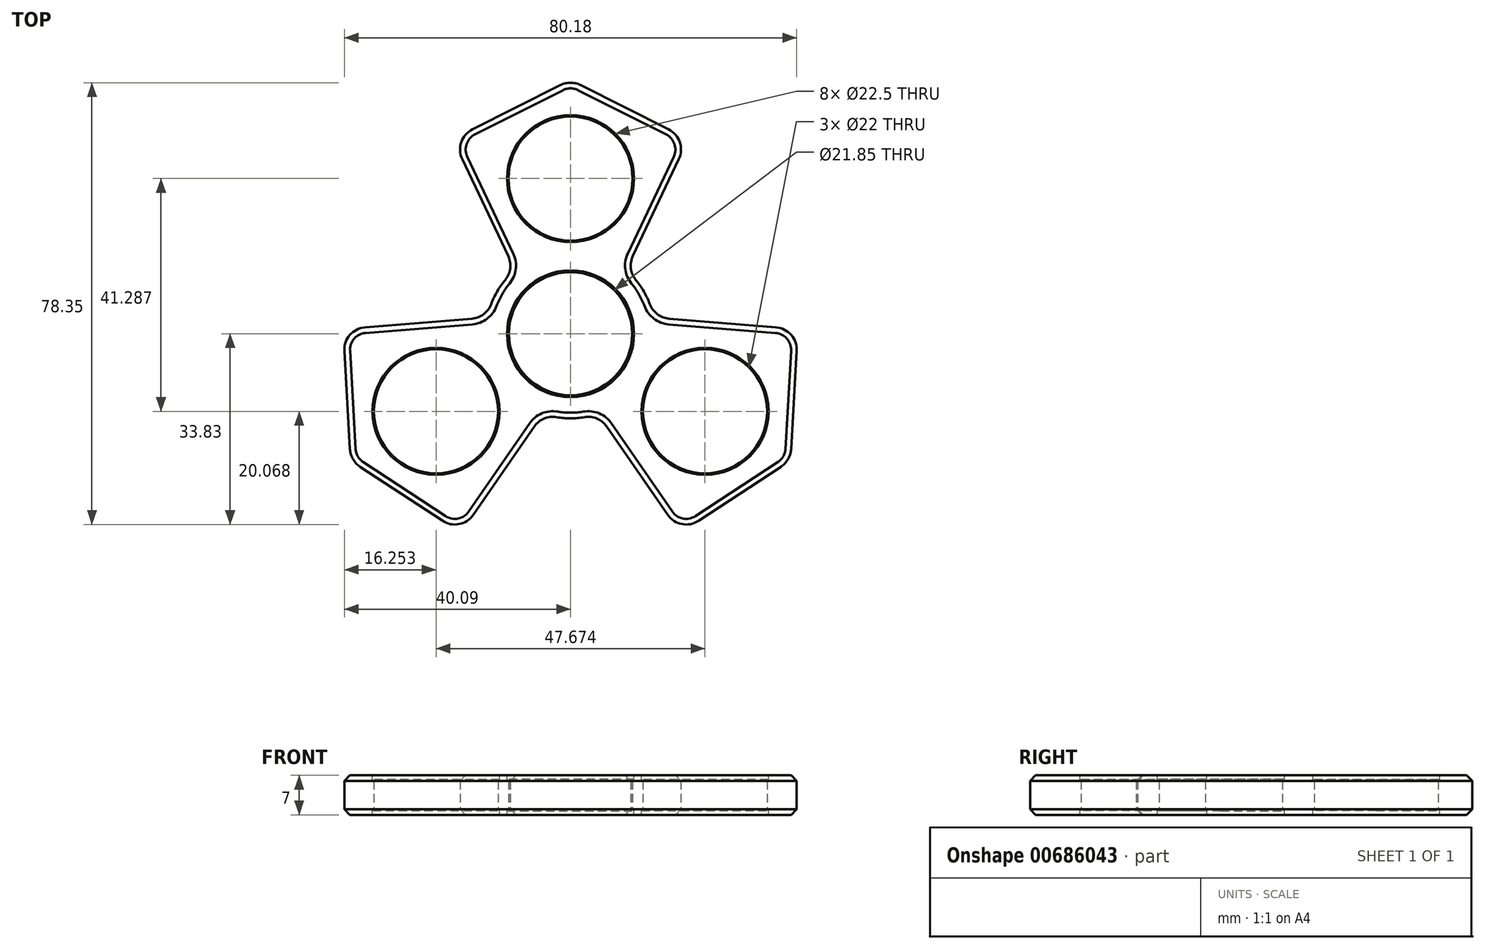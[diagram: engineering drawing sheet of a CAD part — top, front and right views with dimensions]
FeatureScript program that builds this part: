
annotation { "Feature Type Name" : "Feature", "Feature Type Description" : "" }
export const myFeature = defineFeature(function(context is Context, id is Id, definition is map)
    precondition{}
    {
        {
            var Q0;
            Q0=qCreatedBy(makeId("Top.planeOp"),FACE);
            var sketch = newSketch(context, id + "F0", { "sketchPlane" : qUnion([Q0])});
            skCircle(sketch, "E0", {"center": v(0, 0) * mm, "radius": 4 * mm});
            skCircle(sketch, "E1", {"center": v(0, 0) * mm, "radius": 45 * mm, "construction": true});
            skCircle(sketch, "E2", {"center": v(0, 27.52) * mm, "radius": 4 * mm});
            skLineSegment(sketch, "E3", {"start": v(0, 45) * mm, "end": v(-20.87, 34.5) * mm});
            skLineSegment(sketch, "E4", {"start": v(-20.87, 34.5) * mm, "end": v(-9.86, 11.3) * mm});
            skLineSegment(sketch, "E5.MirrorCS", {"start": v(0, 45) * mm, "end": v(20.87, 34.5) * mm});
            skLineSegment(sketch, "E6.MirrorCS", {"start": v(20.87, 34.5) * mm, "end": v(9.86, 11.3) * mm});
            skCircle(sketch, "E7", {"center": v(0, 0) * mm, "radius": 15 * mm});
            skCircle(sketch, "E8.1.1", {"center": v(0, 27.52) * mm, "radius": 11 * mm});
            skCircle(sketch, "E9", {"center": v(0, 0) * mm, "radius": 10.93 * mm});
            skLineSegment(sketch, "E10.1.0", {"start": v(-40.3, 0.83) * mm, "end": v(-14.72, 2.89) * mm});
            skLineSegment(sketch, "E10.1.1", {"start": v(-38.97, -22.5) * mm, "end": v(-40.3, 0.83) * mm});
            skLineSegment(sketch, "E10.1.2", {"start": v(-38.97, -22.5) * mm, "end": v(-19.43, -35.32) * mm});
            skLineSegment(sketch, "E10.1.3", {"start": v(-19.43, -35.32) * mm, "end": v(-4.86, -14.2) * mm});
            skCircle(sketch, "E10.1.4", {"center": v(-23.84, -13.76) * mm, "radius": 11 * mm});
            skCircle(sketch, "E10.1.5", {"center": v(-23.84, -13.76) * mm, "radius": 4 * mm});
            skLineSegment(sketch, "E10.2.0", {"start": v(19.43, -35.32) * mm, "end": v(4.86, -14.2) * mm});
            skLineSegment(sketch, "E10.2.1", {"start": v(38.97, -22.5) * mm, "end": v(19.43, -35.32) * mm});
            skLineSegment(sketch, "E10.2.2", {"start": v(38.97, -22.5) * mm, "end": v(40.3, 0.83) * mm});
            skLineSegment(sketch, "E10.2.3", {"start": v(40.3, 0.83) * mm, "end": v(14.72, 2.89) * mm});
            skCircle(sketch, "E10.2.4", {"center": v(23.84, -13.76) * mm, "radius": 11 * mm});
            skCircle(sketch, "E10.2.5", {"center": v(23.84, -13.76) * mm, "radius": 4 * mm});
            skSolve(sketch);
        }
        {
            var Q0;
            Q0=qSketchRegion(id+"F0",true);
            extrude(context, id + "F1", {"entities" : qUnion([Q0]), "depth" : 7 * mm, "offsetDistance" : 25 * mm});
        }
        {
            var Q0;
            Q0=makeQuery(id+"F1.opExtrude","SWEPT_EDGE",EDGE,{"disambiguationData":[OSD([sQuery(id+"F0.wireOp",EDGE,"472c968c-1dea-4124-b28b-64800f5080bb.1.0"),sQuery(id+"F0.wireOp",EDGE,"472c968c-1dea-4124-b28b-64800f5080bb.1.1")])]});
            var Q1;
            Q1=makeQuery(id+"F1.opExtrude","SWEPT_EDGE",EDGE,{"disambiguationData":[OSD([sQuery(id+"F0.wireOp",EDGE,"472c968c-1dea-4124-b28b-64800f5080bb.2.2"),sQuery(id+"F0.wireOp",EDGE,"472c968c-1dea-4124-b28b-64800f5080bb.2.3")])]});
            var Q2;
            Q2=makeQuery(id+"F1.opExtrude","SWEPT_EDGE",EDGE,{"disambiguationData":[OSD([sQuery(id+"F0.wireOp",EDGE,"472c968c-1dea-4124-b28b-64800f5080bb.2.0"),sQuery(id+"F0.wireOp",EDGE,"472c968c-1dea-4124-b28b-64800f5080bb.2.2")])]});
            var Q3;
            Q3=makeQuery(id+"F1.opExtrude","SWEPT_EDGE",EDGE,{"disambiguationData":[OSD([sQuery(id+"F0.wireOp",EDGE,"472c968c-1dea-4124-b28b-64800f5080bb.2.0"),sQuery(id+"F0.wireOp",EDGE,"472c968c-1dea-4124-b28b-64800f5080bb.2.1")])]});
            var Q4;
            Q4=makeQuery(id+"F1.opExtrude","SWEPT_EDGE",EDGE,{"disambiguationData":[OSD([sQuery(id+"F0.wireOp",EDGE,"472c968c-1dea-4124-b28b-64800f5080bb.2.1"),sQuery(id+"F0.wireOp",EDGE,"E7")])]});
            var Q5;
            Q5=makeQuery(id+"F1.opExtrude","SWEPT_EDGE",EDGE,{"disambiguationData":[OSD([sQuery(id+"F0.wireOp",EDGE,"E6.MirrorCS"),sQuery(id+"F0.wireOp",EDGE,"E7")])]});
            var Q6;
            Q6=makeQuery(id+"F1.opExtrude","SWEPT_EDGE",EDGE,{"disambiguationData":[OSD([sQuery(id+"F0.wireOp",EDGE,"E5.MirrorCS"),sQuery(id+"F0.wireOp",EDGE,"E6.MirrorCS")])]});
            var Q7;
            Q7=makeQuery(id+"F1.opExtrude","SWEPT_EDGE",EDGE,{"disambiguationData":[OSD([sQuery(id+"F0.wireOp",EDGE,"E3"),sQuery(id+"F0.wireOp",EDGE,"E5.MirrorCS")])]});
            var Q8;
            Q8=makeQuery(id+"F1.opExtrude","SWEPT_EDGE",EDGE,{"disambiguationData":[OSD([sQuery(id+"F0.wireOp",EDGE,"E3"),sQuery(id+"F0.wireOp",EDGE,"E4")])]});
            var Q9;
            Q9=makeQuery(id+"F1.opExtrude","SWEPT_EDGE",EDGE,{"disambiguationData":[OSD([sQuery(id+"F0.wireOp",EDGE,"E4"),sQuery(id+"F0.wireOp",EDGE,"E7")])]});
            var Q10;
            Q10=makeQuery(id+"F1.opExtrude","SWEPT_EDGE",EDGE,{"disambiguationData":[OSD([sQuery(id+"F0.wireOp",EDGE,"472c968c-1dea-4124-b28b-64800f5080bb.1.3"),sQuery(id+"F0.wireOp",EDGE,"E7")])]});
            var Q11;
            Q11=makeQuery(id+"F1.opExtrude","SWEPT_EDGE",EDGE,{"disambiguationData":[OSD([sQuery(id+"F0.wireOp",EDGE,"472c968c-1dea-4124-b28b-64800f5080bb.1.2"),sQuery(id+"F0.wireOp",EDGE,"472c968c-1dea-4124-b28b-64800f5080bb.1.3")])]});
            var Q12;
            Q12=makeQuery(id+"F1.opExtrude","SWEPT_EDGE",EDGE,{"disambiguationData":[OSD([sQuery(id+"F0.wireOp",EDGE,"472c968c-1dea-4124-b28b-64800f5080bb.1.0"),sQuery(id+"F0.wireOp",EDGE,"472c968c-1dea-4124-b28b-64800f5080bb.1.2")])]});
            var Q13;
            Q13=makeQuery(id+"F1.opExtrude","SWEPT_EDGE",EDGE,{"disambiguationData":[OSD([sQuery(id+"F0.wireOp",EDGE,"472c968c-1dea-4124-b28b-64800f5080bb.1.1"),sQuery(id+"F0.wireOp",EDGE,"E7")])]});
            var Q14;
            Q14=makeQuery(id+"F1.opExtrude","SWEPT_EDGE",EDGE,{"disambiguationData":[OSD([sQuery(id+"F0.wireOp",EDGE,"472c968c-1dea-4124-b28b-64800f5080bb.2.3"),sQuery(id+"F0.wireOp",EDGE,"E7")])]});
            var Q15;
            Q15=makeQuery(id+"F1.opExtrude","SWEPT_EDGE",EDGE,{"disambiguationData":[OSD([sQuery(id+"F0.wireOp",EDGE,"E10.2.0"),sQuery(id+"F0.wireOp",EDGE,"E10.2.1")])]});
            var Q16;
            Q16=makeQuery(id+"F1.opExtrude","SWEPT_EDGE",EDGE,{"disambiguationData":[OSD([sQuery(id+"F0.wireOp",EDGE,"E10.2.1"),sQuery(id+"F0.wireOp",EDGE,"E10.2.2")])]});
            var Q17;
            Q17=makeQuery(id+"F1.opExtrude","SWEPT_EDGE",EDGE,{"disambiguationData":[OSD([sQuery(id+"F0.wireOp",EDGE,"E10.2.2"),sQuery(id+"F0.wireOp",EDGE,"E10.2.3")])]});
            var Q18;
            Q18=makeQuery(id+"F1.opExtrude","SWEPT_EDGE",EDGE,{"disambiguationData":[OSD([sQuery(id+"F0.wireOp",EDGE,"E10.1.2"),sQuery(id+"F0.wireOp",EDGE,"E10.1.3")])]});
            var Q19;
            Q19=makeQuery(id+"F1.opExtrude","SWEPT_EDGE",EDGE,{"disambiguationData":[OSD([sQuery(id+"F0.wireOp",EDGE,"E10.1.1"),sQuery(id+"F0.wireOp",EDGE,"E10.1.2")])]});
            var Q20;
            Q20=makeQuery(id+"F1.opExtrude","SWEPT_EDGE",EDGE,{"disambiguationData":[OSD([sQuery(id+"F0.wireOp",EDGE,"E10.1.0"),sQuery(id+"F0.wireOp",EDGE,"E10.1.1")])]});
            fillet(context, id + "F2", {"entities" : qUnion([Q0, Q1, Q2, Q3, Q4, Q5, Q6, Q7, Q8, Q9, Q10, Q11, Q12, Q13, Q14, Q15, Q16, Q17, Q18, Q19, Q20]), "radius" : 4 * mm, "tangentPropagation" : true, "allowEdgeOverflow" : false});
        }
        {
            var Q0;
            Q0=makeQuery(id+"F1.opExtrude","CAP_EDGE",EDGE,{"disambiguationData":[OSD([sQuery(id+"F0.wireOp",EDGE,"E4")])],"isStart":false});
            var Q1;
            Q1=makeQuery(id+"F1.opExtrude","CAP_EDGE",EDGE,{"disambiguationData":[OSD([sQuery(id+"F0.wireOp",EDGE,"E4")])],"isStart":true});
            var Q2;
            Q2=makeQuery(id+"F1.opExtrude","CAP_EDGE",EDGE,{"disambiguationData":[OSD([sQuery(id+"F0.wireOp",EDGE,"E10.1.1")])],"isStart":false});
            var Q3;
            Q3=makeQuery(id+"F1.opExtrude","CAP_EDGE",EDGE,{"disambiguationData":[OSD([sQuery(id+"F0.wireOp",EDGE,"E10.1.2")])],"isStart":false});
            var Q4;
            Q4=makeQuery(id+"F1.opExtrude","CAP_FACE",FACE,{"disambiguationData":[OSD([sQuery(id+"F0.wireOp",EDGE,"E3"),sQuery(id+"F0.wireOp",EDGE,"E4"),sQuery(id+"F0.wireOp",EDGE,"E5.MirrorCS"),sQuery(id+"F0.wireOp",EDGE,"E6.MirrorCS"),sQuery(id+"F0.wireOp",EDGE,"E7"),sQuery(id+"F0.wireOp",EDGE,"E8.1.1"),sQuery(id+"F0.wireOp",EDGE,"E9"),sQuery(id+"F0.wireOp",EDGE,"E10.1.0"),sQuery(id+"F0.wireOp",EDGE,"E10.1.1"),sQuery(id+"F0.wireOp",EDGE,"E10.1.2"),sQuery(id+"F0.wireOp",EDGE,"E10.1.3"),sQuery(id+"F0.wireOp",EDGE,"E10.1.4"),sQuery(id+"F0.wireOp",EDGE,"E10.2.0"),sQuery(id+"F0.wireOp",EDGE,"E10.2.1"),sQuery(id+"F0.wireOp",EDGE,"E10.2.2"),sQuery(id+"F0.wireOp",EDGE,"E10.2.3"),sQuery(id+"F0.wireOp",EDGE,"E10.2.4")])],"isStart":false});
            var Q5;
            Q5=makeQuery(id+"F1.opExtrude","CAP_FACE",FACE,{"disambiguationData":[OSD([sQuery(id+"F0.wireOp",EDGE,"E3"),sQuery(id+"F0.wireOp",EDGE,"E4"),sQuery(id+"F0.wireOp",EDGE,"E5.MirrorCS"),sQuery(id+"F0.wireOp",EDGE,"E6.MirrorCS"),sQuery(id+"F0.wireOp",EDGE,"E7"),sQuery(id+"F0.wireOp",EDGE,"E8.1.1"),sQuery(id+"F0.wireOp",EDGE,"E9"),sQuery(id+"F0.wireOp",EDGE,"E10.1.0"),sQuery(id+"F0.wireOp",EDGE,"E10.1.1"),sQuery(id+"F0.wireOp",EDGE,"E10.1.2"),sQuery(id+"F0.wireOp",EDGE,"E10.1.3"),sQuery(id+"F0.wireOp",EDGE,"E10.1.4"),sQuery(id+"F0.wireOp",EDGE,"E10.2.0"),sQuery(id+"F0.wireOp",EDGE,"E10.2.1"),sQuery(id+"F0.wireOp",EDGE,"E10.2.2"),sQuery(id+"F0.wireOp",EDGE,"E10.2.3"),sQuery(id+"F0.wireOp",EDGE,"E10.2.4")])],"isStart":true});
            chamfer(context, id + "F3", {"entities" : qUnion([Q0, Q1, Q2, Q3, Q4, Q5]), "width" : 1 * mm, "tangentPropagation" : true});
        }
        {
            var Q0;
            Q0=makeQuery(id+"F1.opExtrude","CAP_FACE",FACE,{"disambiguationData":[OSD([sQuery(id+"F0.wireOp",EDGE,"E3"),sQuery(id+"F0.wireOp",EDGE,"E4"),sQuery(id+"F0.wireOp",EDGE,"E5.MirrorCS"),sQuery(id+"F0.wireOp",EDGE,"E6.MirrorCS"),sQuery(id+"F0.wireOp",EDGE,"472c968c-1dea-4124-b28b-64800f5080bb.1.0"),sQuery(id+"F0.wireOp",EDGE,"472c968c-1dea-4124-b28b-64800f5080bb.1.1"),sQuery(id+"F0.wireOp",EDGE,"472c968c-1dea-4124-b28b-64800f5080bb.1.2"),sQuery(id+"F0.wireOp",EDGE,"472c968c-1dea-4124-b28b-64800f5080bb.1.3"),sQuery(id+"F0.wireOp",EDGE,"472c968c-1dea-4124-b28b-64800f5080bb.2.0"),sQuery(id+"F0.wireOp",EDGE,"472c968c-1dea-4124-b28b-64800f5080bb.2.1"),sQuery(id+"F0.wireOp",EDGE,"472c968c-1dea-4124-b28b-64800f5080bb.2.2"),sQuery(id+"F0.wireOp",EDGE,"472c968c-1dea-4124-b28b-64800f5080bb.2.3"),sQuery(id+"F0.wireOp",EDGE,"E7"),sQuery(id+"F0.wireOp",EDGE,"7CMQf4OQ-Sror-fCje-mLh9-7LnnwRFnTUJV"),sQuery(id+"F0.wireOp",EDGE,"E8.1.1"),sQuery(id+"F0.wireOp",EDGE,"E8.2.1"),sQuery(id+"F0.wireOp",EDGE,"E9")])],"isStart":false});
            var sketch = newSketch(context, id + "F4", { "sketchPlane" : qUnion([Q0])});
            skCircle(sketch, "E11", {"center": v(0, 27.52) * mm, "radius": 11.25 * mm});
            skCircle(sketch, "E12", {"center": v(23.84, -13.76) * mm, "radius": 11.25 * mm});
            skCircle(sketch, "E13", {"center": v(-23.84, -13.76) * mm, "radius": 11.25 * mm});
            skCircle(sketch, "E14", {"center": v(-23.84, -13.76) * mm, "radius": 12.02 * mm});
            skCircle(sketch, "E15", {"center": v(23.84, -13.76) * mm, "radius": 12.02 * mm});
            skCircle(sketch, "E16", {"center": v(0, 27.52) * mm, "radius": 12.13 * mm});
            skCircle(sketch, "E17", {"center": v(0, 0) * mm, "radius": 11.25 * mm});
            skCircle(sketch, "E18", {"center": v(0, 0) * mm, "radius": 12.44 * mm});
            skSolve(sketch);
        }
        {
            var Q0;
            Q0=makeQuery(id+"F4.imprint","IMPRINT",FACE,{"disambiguationData":[TD([[makeQuery(id+"F4.imprint","IMPRINT",EDGE,{"derivedFrom":sQuery(id+"F4.wireOp",EDGE,"E17")}),-1.0]])]});
            var Q1;
            Q1=makeQuery(id+"F4.imprint","IMPRINT",FACE,{"disambiguationData":[TD([[makeQuery(id+"F4.imprint","IMPRINT",EDGE,{"derivedFrom":sQuery(id+"F4.wireOp",EDGE,"E11")}),-1.0]])]});
            var Q2;
            Q2=makeQuery(id+"F4.imprint","IMPRINT",FACE,{"disambiguationData":[TD([[makeQuery(id+"F4.imprint","IMPRINT",EDGE,{"derivedFrom":sQuery(id+"F4.wireOp",EDGE,"E13")}),-1.0]])]});
            var Q3;
            Q3=makeQuery(id+"F4.imprint","IMPRINT",FACE,{"disambiguationData":[TD([[makeQuery(id+"F4.imprint","IMPRINT",EDGE,{"derivedFrom":sQuery(id+"F4.wireOp",EDGE,"E12")}),-1.0]])]});
            extrude(context, id + "F5", {"entities" : qUnion([Q0, Q1, Q2, Q3]), "operationType" : NewBodyOperationType.ADD, "oppositeDirection" : true, "depth" : 7 * mm, "offsetDistance" : 25 * mm});
        }
    });
